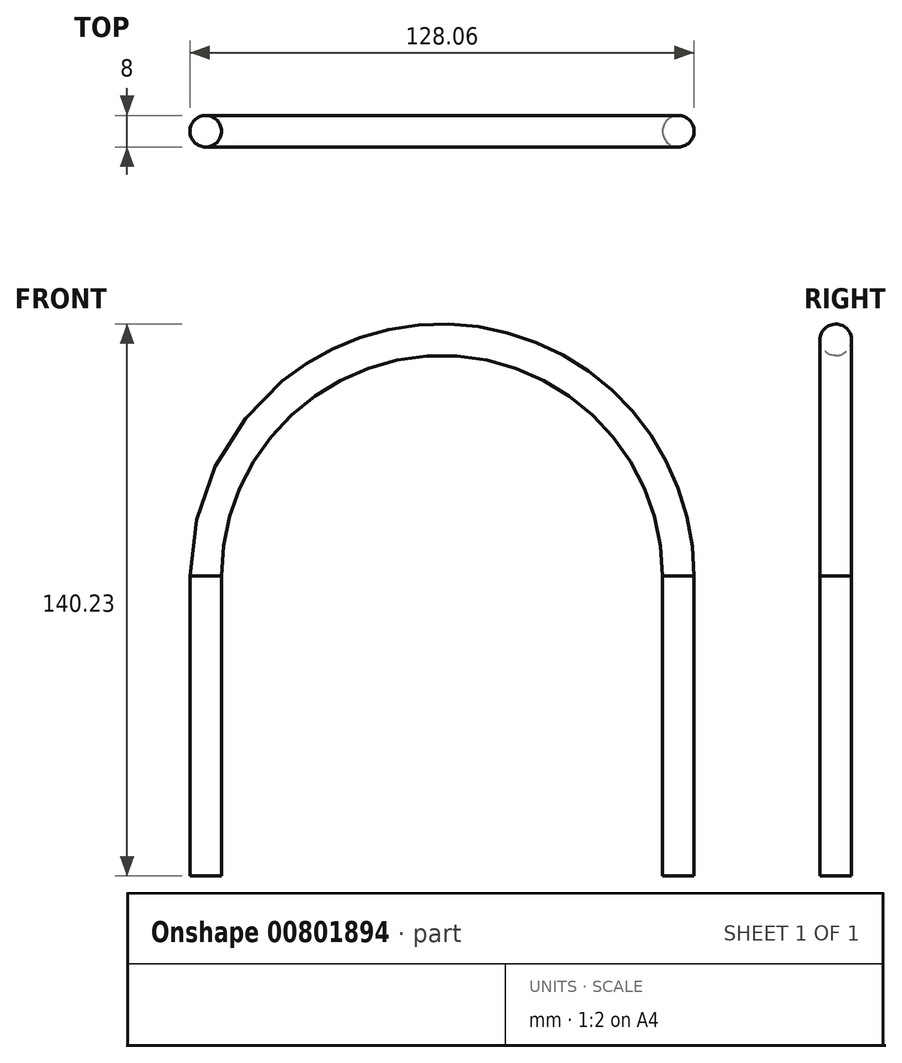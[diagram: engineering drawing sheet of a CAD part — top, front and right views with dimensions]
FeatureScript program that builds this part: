
annotation { "Feature Type Name" : "Feature", "Feature Type Description" : "" }
export const myFeature = defineFeature(function(context is Context, id is Id, definition is map)
    precondition{}
    {
        {
            var Q0;
            Q0=qCreatedBy(makeId("Top.planeOp"),FACE);
            var sketch = newSketch(context, id + "F0", { "sketchPlane" : qUnion([Q0])});
            skCircle(sketch, "E0", {"center": v(0, 0) * mm, "radius": 4 * mm});
            skCircle(sketch, "E1", {"center": v(-120.06, 0) * mm, "radius": 4 * mm});
            skSolve(sketch);
        }
        {
            var Q0;
            Q0=qSketchRegion(id+"F0",true);
            extrude(context, id + "F1", {"entities" : qUnion([Q0]), "depth" : 76.2 * mm, "offsetDistance" : 25 * mm});
        }
        {
            var Q0;
            Q0=makeQuery(id+"F1.opExtrude","CAP_FACE",FACE,{"disambiguationData":[OSD([sQuery(id+"F0.wireOp",EDGE,"E1")])],"isStart":false});
            var sketch = newSketch(context, id + "F2", { "sketchPlane" : qUnion([Q0])});
            skLineSegment(sketch, "E2", {"start": v(-120.06, 0) * mm, "end": v(0, 0) * mm, "construction": true});
            skLineSegment(sketch, "E3", {"start": v(-60.03, 0) * mm, "end": v(-60.03, -24.31) * mm, "construction": true});
            skCircle(sketch, "E4", {"center": v(-120.06, 0) * mm, "radius": 4 * mm});
            skSolve(sketch);
        }
        {
            var Q0;
            Q0=qSketchRegion(id+"F2",true);
            var Q1;
            Q1=sQuery(id+"F2.wireOp",EDGE,"E3");
            revolve(context, id + "F3", {"entities" : qUnion([Q0]), "axis" : qUnion([Q1]), "revolveType" : RevolveType.ONE_DIRECTION, "oppositeDirection" : true, "angle" : 180 * degree});
        }
    });
